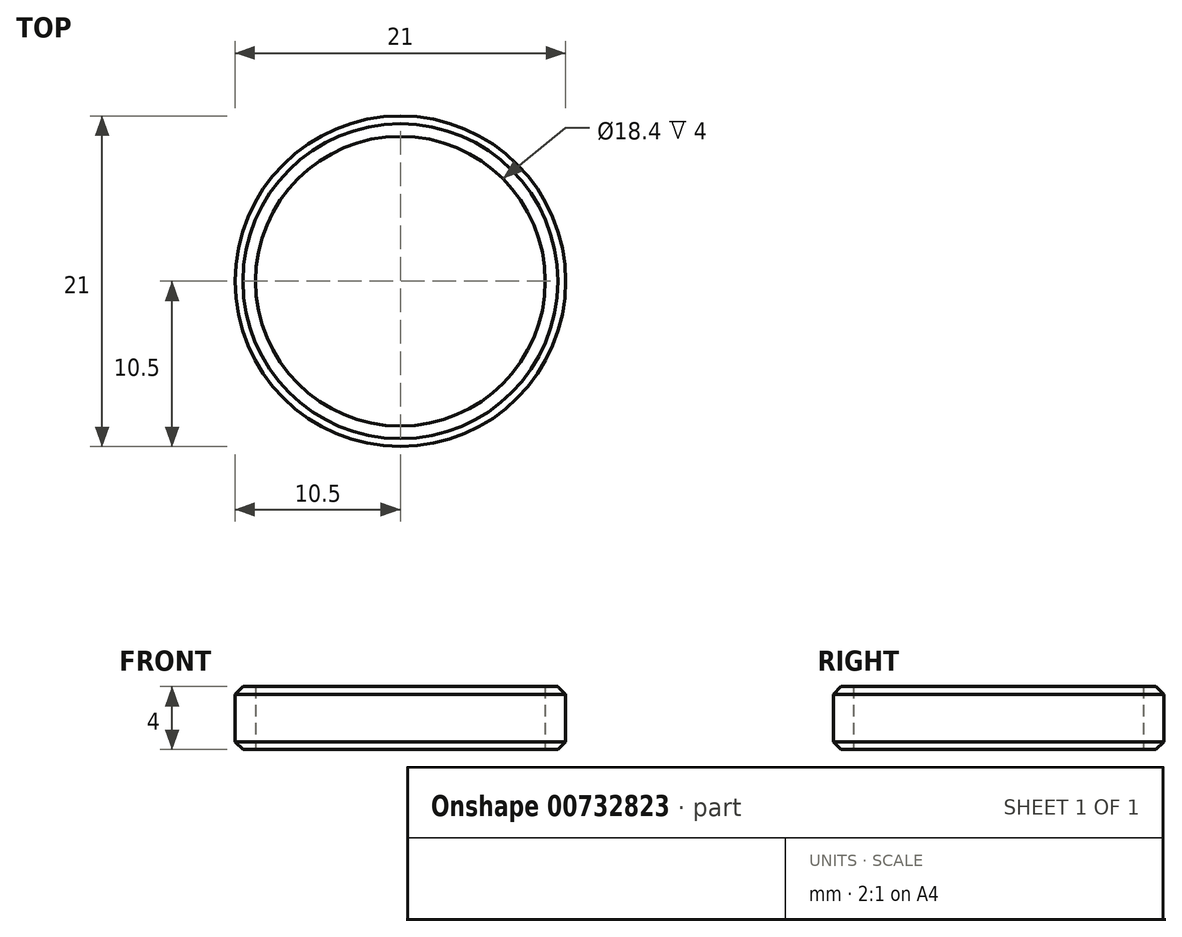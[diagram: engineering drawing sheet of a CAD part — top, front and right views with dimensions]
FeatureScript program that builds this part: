
annotation { "Feature Type Name" : "Feature", "Feature Type Description" : "" }
export const myFeature = defineFeature(function(context is Context, id is Id, definition is map)
    precondition{}
    {
        {
            var Q0;
            Q0=qCreatedBy(makeId("Top.planeOp"),FACE);
            var sketch = newSketch(context, id + "F0", { "sketchPlane" : qUnion([Q0])});
            skCircle(sketch, "E0", {"center": v(0, 0) * mm, "radius": 10.5 * mm});
            skCircle(sketch, "E1", {"center": v(0, 0) * mm, "radius": 9.2 * mm});
            skSolve(sketch);
        }
        {
            var Q0;
            Q0=makeQuery(id+"F0.imprint","IMPRINT",FACE,{"disambiguationData":[TD([[makeQuery(id+"F0.imprint","IMPRINT",EDGE,{"derivedFrom":sQuery(id+"F0.wireOp",EDGE,"E0")}),1.0]])]});
            extrude(context, id + "F1", {"entities" : qUnion([Q0]), "depth" : 4 * mm, "offsetDistance" : 25 * mm});
        }
        {
            var Q0;
            Q0=makeQuery(id+"F1.opExtrude","CAP_EDGE",EDGE,{"disambiguationData":[OSD([sQuery(id+"F0.wireOp",EDGE,"E0")])],"isStart":true});
            var Q1;
            Q1=makeQuery(id+"F1.opExtrude","CAP_EDGE",EDGE,{"disambiguationData":[OSD([sQuery(id+"F0.wireOp",EDGE,"E0")])],"isStart":false});
            chamfer(context, id + "F2", {"entities" : qUnion([Q0, Q1]), "width" : .5 * mm, "tangentPropagation" : true});
        }
    });
